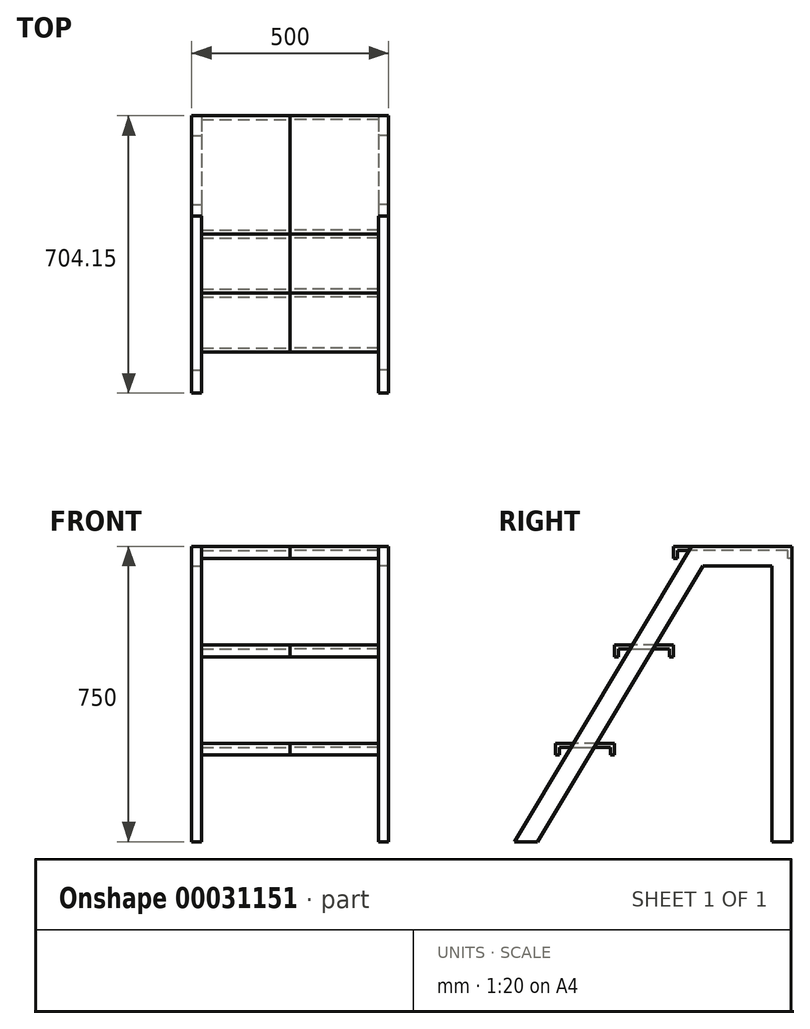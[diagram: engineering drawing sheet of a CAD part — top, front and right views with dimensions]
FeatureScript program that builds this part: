
annotation { "Feature Type Name" : "Feature", "Feature Type Description" : "" }
export const myFeature = defineFeature(function(context is Context, id is Id, definition is map)
    precondition{}
    {
        {
            var Q0;
            Q0=qCreatedBy(makeId("Right.planeOp"),FACE);
            var sketch = newSketch(context, id + "F0", { "sketchPlane" : qUnion([Q0])});
            skLineSegment(sketch, "E0", {"start": v(150, 250) * mm, "end": v(0, 250) * mm});
            skLineSegment(sketch, "E1", {"start": v(0, 250) * mm, "end": v(0, 220) * mm});
            skLineSegment(sketch, "E2", {"start": v(0, 220) * mm, "end": v(10, 220) * mm});
            skLineSegment(sketch, "E3", {"start": v(10, 220) * mm, "end": v(10, 240) * mm});
            skLineSegment(sketch, "E4", {"start": v(10, 240) * mm, "end": v(140, 240) * mm});
            skLineSegment(sketch, "E5", {"start": v(140, 240) * mm, "end": v(140, 220) * mm});
            skLineSegment(sketch, "E6", {"start": v(140, 220) * mm, "end": v(150, 220) * mm});
            skLineSegment(sketch, "E7", {"start": v(150, 220) * mm, "end": v(150, 250) * mm});
            skLineSegment(sketch, "E8.1.1.0", {"start": v(160, 490) * mm, "end": v(290, 490) * mm});
            skLineSegment(sketch, "E8.1.1.1", {"start": v(300, 470) * mm, "end": v(300, 500) * mm});
            skLineSegment(sketch, "E8.1.1.2", {"start": v(160, 470) * mm, "end": v(160, 490) * mm});
            skLineSegment(sketch, "E8.1.1.3", {"start": v(290, 490) * mm, "end": v(290, 470) * mm});
            skLineSegment(sketch, "E8.1.1.4", {"start": v(150, 500) * mm, "end": v(150, 470) * mm});
            skLineSegment(sketch, "E8.1.1.5", {"start": v(300, 500) * mm, "end": v(150, 500) * mm});
            skLineSegment(sketch, "E8.1.1.6", {"start": v(290, 470) * mm, "end": v(300, 470) * mm});
            skLineSegment(sketch, "E8.1.1.7", {"start": v(150, 470) * mm, "end": v(160, 470) * mm});
            skLineSegment(sketch, "E9", {"start": v(300, 720) * mm, "end": v(300, 750) * mm});
            skLineSegment(sketch, "E10", {"start": v(300, 750) * mm, "end": v(600, 750) * mm});
            skLineSegment(sketch, "E11", {"start": v(600, 750) * mm, "end": v(600, 720) * mm});
            skLineSegment(sketch, "E12", {"start": v(600, 720) * mm, "end": v(590, 720) * mm});
            skLineSegment(sketch, "E13", {"start": v(590, 720) * mm, "end": v(590, 740) * mm});
            skLineSegment(sketch, "E14", {"start": v(590, 740) * mm, "end": v(310, 740) * mm});
            skLineSegment(sketch, "E15", {"start": v(310, 740) * mm, "end": v(310, 720) * mm});
            skLineSegment(sketch, "E16", {"start": v(310, 720) * mm, "end": v(300, 720) * mm});
            skSolve(sketch);
        }
        {
            var Q0;
            Q0=qSketchRegion(id+"F0",true);
            extrude(context, id + "F1", {"entities" : qUnion([Q0]), "depth" : 225 * mm});
        }
        {
            var Q0;
            Q0=makeQuery(id+"F1.opExtrude","CAP_FACE",FACE,{"disambiguationData":[OSD([sQuery(id+"F0.wireOp",EDGE,"E0"),sQuery(id+"F0.wireOp",EDGE,"E1"),sQuery(id+"F0.wireOp",EDGE,"E2"),sQuery(id+"F0.wireOp",EDGE,"E3"),sQuery(id+"F0.wireOp",EDGE,"E4"),sQuery(id+"F0.wireOp",EDGE,"E5"),sQuery(id+"F0.wireOp",EDGE,"E6"),sQuery(id+"F0.wireOp",EDGE,"E7")])],"isStart":false});
            var sketch = newSketch(context, id + "F2", { "sketchPlane" : qUnion([Q0])});
            skLineSegment(sketch, "E17", {"start": v(600, 750) * mm, "end": v(600, 0) * mm});
            skLineSegment(sketch, "E18", {"start": v(600, 0) * mm, "end": v(550, 0) * mm});
            skLineSegment(sketch, "E19", {"start": v(550, 0) * mm, "end": v(550, 700) * mm});
            skLineSegment(sketch, "E20", {"start": v(550, 700) * mm, "end": v(374.15, 700) * mm});
            skLineSegment(sketch, "E21", {"start": v(374.15, 700) * mm, "end": v(-45.85, 0) * mm});
            skLineSegment(sketch, "E22", {"start": v(-45.85, 0) * mm, "end": v(-104.15, 0) * mm});
            skLineSegment(sketch, "E23", {"start": v(-104.15, 0) * mm, "end": v(345.85, 750) * mm});
            skLineSegment(sketch, "E24", {"start": v(345.85, 750) * mm, "end": v(600, 750) * mm});
            skLineSegment(sketch, "E25", {"start": v(203.56, 512.86) * mm, "end": v(246.44, 487.14) * mm, "construction": true});
            skLineSegment(sketch, "E26", {"start": v(374.15, 700) * mm, "end": v(374.15, 750) * mm, "construction": true});
            skLineSegment(sketch, "E27", {"start": v(-75, 0) * mm, "end": v(225, 500) * mm, "construction": true});
            skPoint(sketch, "E28", {"position": v(75, 250) * mm});
            skSolve(sketch);
        }
        {
            var Q0;
            Q0=qSketchRegion(id+"F2",true);
            extrude(context, id + "F3", {"entities" : qUnion([Q0]), "operationType" : NewBodyOperationType.ADD, "depth" : 25 * mm});
        }
        {
            var Q0;
            Q0=makeQuery(id+"F1.opExtrude","SWEPT_BODY",BODY,{"disambiguationData":[OSD([sQuery(id+"F0.wireOp",EDGE,"E0"),sQuery(id+"F0.wireOp",EDGE,"E1"),sQuery(id+"F0.wireOp",EDGE,"E2"),sQuery(id+"F0.wireOp",EDGE,"E3"),sQuery(id+"F0.wireOp",EDGE,"E4"),sQuery(id+"F0.wireOp",EDGE,"E5"),sQuery(id+"F0.wireOp",EDGE,"E6"),sQuery(id+"F0.wireOp",EDGE,"E7")])]});
            var Q1;
            Q1=qCreatedBy(makeId("Right.planeOp"),FACE);
            mirror(context, id + "F4", {"entities" : qUnion([Q0]), "mirrorPlane" : qUnion([Q1])});
        }
    });
